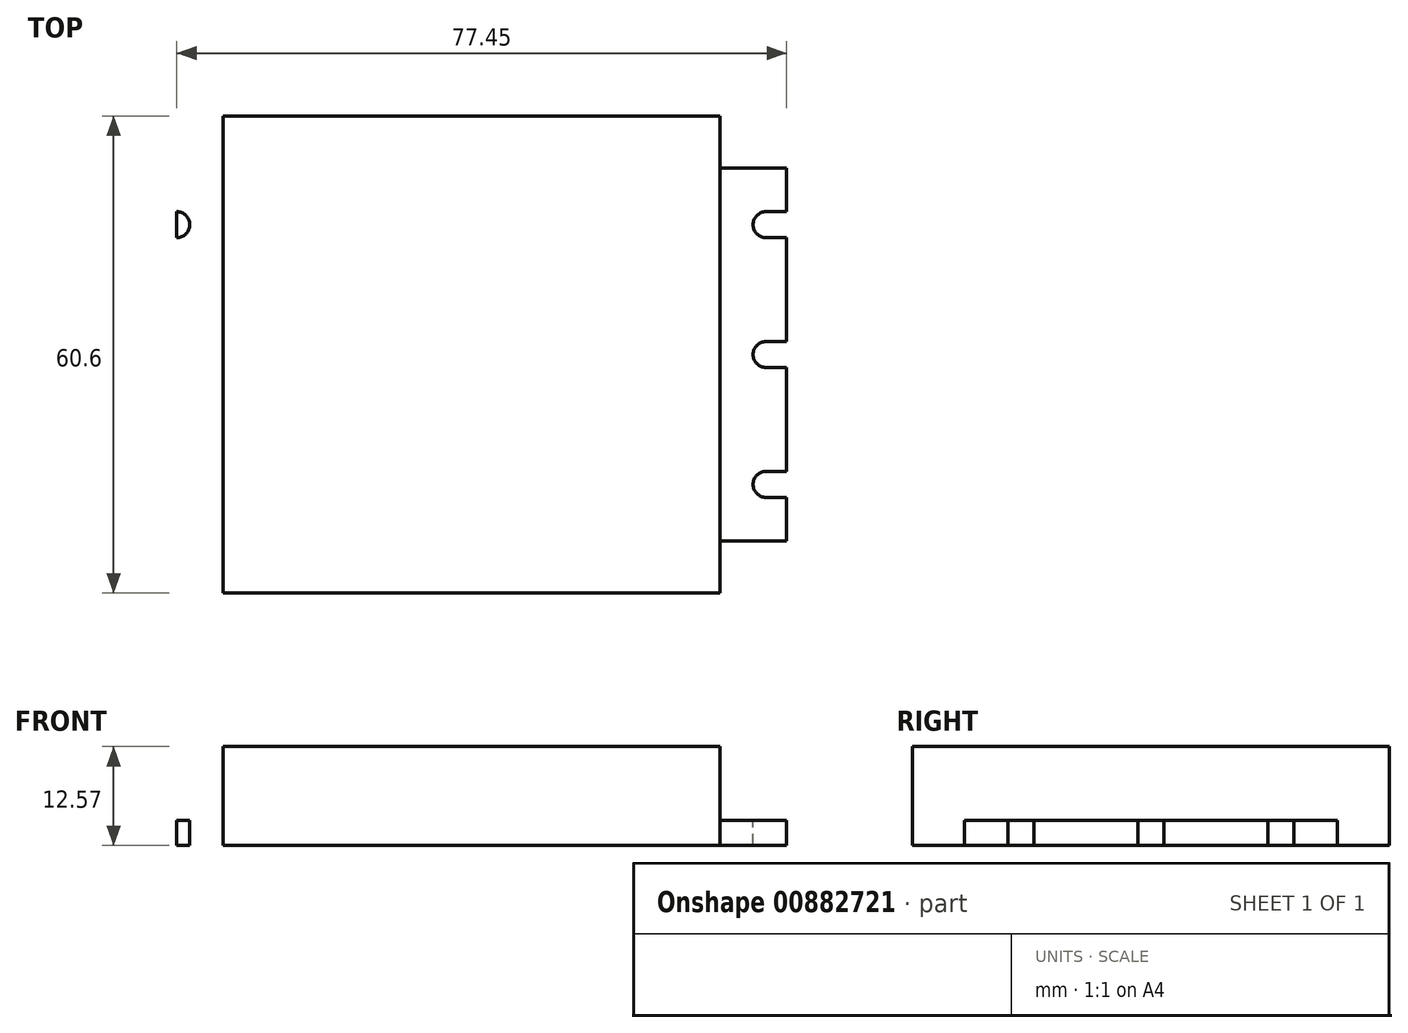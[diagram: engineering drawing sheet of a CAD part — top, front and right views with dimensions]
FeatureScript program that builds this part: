
annotation { "Feature Type Name" : "Feature", "Feature Type Description" : "" }
export const myFeature = defineFeature(function(context is Context, id is Id, definition is map)
    precondition{}
    {
        {
            var Q0;
            Q0=qCreatedBy(makeId("Top.planeOp"),FACE);
            var sketch = newSketch(context, id + "F0", { "sketchPlane" : qUnion([Q0])});
            skLineSegment(sketch, "E0.bottom", {"start": v(31.57, 30.3) * mm, "end": v(-31.57, 30.3) * mm});
            skLineSegment(sketch, "E0.top", {"start": v(31.57, -30.3) * mm, "end": v(-31.57, -30.3) * mm});
            skLineSegment(sketch, "E0.left", {"start": v(31.57, 30.3) * mm, "end": v(31.57, -30.3) * mm});
            skLineSegment(sketch, "E0.right", {"start": v(-31.57, 30.3) * mm, "end": v(-31.57, -30.3) * mm});
            skPoint(sketch, "E0.middle", {"position": v(0, 0) * mm});
            skLineSegment(sketch, "E1.bottom", {"start": v(25.4, 25.4) * mm, "end": v(-25.4, 25.4) * mm, "construction": true});
            skLineSegment(sketch, "E1.top", {"start": v(25.4, -25.4) * mm, "end": v(-25.4, -25.4) * mm, "construction": true});
            skLineSegment(sketch, "E1.left", {"start": v(25.4, 25.4) * mm, "end": v(25.4, -25.4) * mm, "construction": true});
            skLineSegment(sketch, "E1.right", {"start": v(-25.4, 25.4) * mm, "end": v(-25.4, -25.4) * mm, "construction": true});
            skSolve(sketch);
        }
        {
            var Q0;
            Q0=makeQuery(id+"F0.imprint","IMPRINT",FACE,{"disambiguationData":[TD([[makeQuery(id+"F0.imprint","IMPRINT",EDGE,{"derivedFrom":sQuery(id+"F0.wireOp",EDGE,"E0.bottom")}),1.0]])]});
            extrude(context, id + "F1", {"entities" : qUnion([Q0]), "depth" : 12.57 * mm, "offsetDistance" : 25 * mm});
        }
        {
            var Q0;
            Q0=makeQuery(id+"F1.opExtrude","SWEPT_FACE",FACE,{"disambiguationData":[OSD([sQuery(id+"F0.wireOp",EDGE,"E0.right")])]});
            var sketch = newSketch(context, id + "F2", { "sketchPlane" : qUnion([Q0])});
            skLineSegment(sketch, "E2.bottom", {"start": v(-23.7, 3.18) * mm, "end": v(23.7, 3.18) * mm});
            skLineSegment(sketch, "E2.top", {"start": v(-23.7, 0) * mm, "end": v(23.7, 0) * mm});
            skLineSegment(sketch, "E2.left", {"start": v(-23.7, 3.18) * mm, "end": v(-23.7, 0) * mm});
            skLineSegment(sketch, "E2.right", {"start": v(23.7, 3.18) * mm, "end": v(23.7, 0) * mm});
            skSolve(sketch);
        }
        {
            var Q0;
            Q0=makeQuery(id+"F2.imprint","IMPRINT",FACE,{"disambiguationData":[TD([[makeQuery(id+"F2.imprint","IMPRINT",EDGE,{"derivedFrom":sQuery(id+"F2.wireOp",EDGE,"E2.bottom")}),-1.0]])]});
            extrude(context, id + "F3", {"entities" : qUnion([Q0]), "operationType" : NewBodyOperationType.ADD, "depth" : 8.45 * mm, "offsetDistance" : 25 * mm});
        }
        {
            var Q0;
            Q0=makeQuery(id+"F1.opExtrude","SWEPT_BODY",BODY,{"disambiguationData":[OSD([sQuery(id+"F0.wireOp",EDGE,"E0.bottom"),sQuery(id+"F0.wireOp",EDGE,"E0.top"),sQuery(id+"F0.wireOp",EDGE,"E0.left"),sQuery(id+"F0.wireOp",EDGE,"E0.right")])]});
            var Q1;
            Q1=qCreatedBy(makeId("Right.planeOp"),FACE);
            mirror(context, id + "F4", {"operationType" : NewBodyOperationType.ADD, "entities" : qUnion([Q0]), "mirrorPlane" : qUnion([Q1])});
        }
        {
            var Q0;
            Q0=makeQuery(id+"F3.opExtrude","SWEPT_FACE",FACE,{"disambiguationData":[OSD([sQuery(id+"F2.wireOp",EDGE,"E2.bottom")])]});
            var sketch = newSketch(context, id + "F5", { "sketchPlane" : qUnion([Q0])});
            skLineSegment(sketch, "E3", {"start": v(-40.02, 1.65) * mm, "end": v(-37.43, 1.65) * mm});
            skLineSegment(sketch, "E4", {"start": v(-37.43, 1.65) * mm, "end": v(-37.43, -1.65) * mm});
            skLineSegment(sketch, "E5", {"start": v(-37.43, -1.65) * mm, "end": v(-40.02, -1.65) * mm});
            skArc(sketch, "E6", {"start": v(-37.43, 1.65) * mm, "mid": v(-35.78, 0) * mm, "end": v(-37.43, -1.65) * mm});
            skLineSegment(sketch, "E7.0.1.0", {"start": v(-40.02, 18.15) * mm, "end": v(-37.43, 18.15) * mm});
            skArc(sketch, "E7.0.1.1", {"start": v(-37.43, 18.15) * mm, "mid": v(-35.78, 16.5) * mm, "end": v(-37.43, 14.85) * mm});
            skLineSegment(sketch, "E7.0.1.2", {"start": v(-37.43, 14.85) * mm, "end": v(-40.02, 14.85) * mm});
            skLineSegment(sketch, "E7.0.1.3", {"start": v(-37.43, 18.15) * mm, "end": v(-37.43, 14.85) * mm});
            skLineSegment(sketch, "E7.direction1", {"start": v(-40.02, -1.65) * mm, "end": v(-37.92, -1.65) * mm, "construction": true});
            skLineSegment(sketch, "E7.direction2", {"start": v(-40.02, -1.65) * mm, "end": v(-40.02, 14.85) * mm, "construction": true});
            skLineSegment(sketch, "E8.MirrorCS", {"start": v(-37.43, -14.85) * mm, "end": v(-40.02, -14.85) * mm});
            skArc(sketch, "E9.MirrorCS", {"start": v(-37.43, -18.15) * mm, "mid": v(-35.78, -16.5) * mm, "end": v(-37.43, -14.85) * mm});
            skLineSegment(sketch, "E10.MirrorCS", {"start": v(-37.43, -18.15) * mm, "end": v(-37.43, -14.85) * mm});
            skLineSegment(sketch, "E11.MirrorCS", {"start": v(-40.02, -18.15) * mm, "end": v(-37.43, -18.15) * mm});
            skLineSegment(sketch, "E12.MirrorCS", {"start": v(37.43, -1.65) * mm, "end": v(40.02, -1.65) * mm});
            skLineSegment(sketch, "E13.MirrorCS", {"start": v(37.43, 1.65) * mm, "end": v(37.43, -1.65) * mm});
            skLineSegment(sketch, "E14.MirrorCS", {"start": v(37.43, -18.15) * mm, "end": v(37.43, -14.85) * mm});
            skLineSegment(sketch, "E15.MirrorCS", {"start": v(37.43, 18.15) * mm, "end": v(37.43, 14.85) * mm});
            skLineSegment(sketch, "E16.MirrorCS", {"start": v(40.02, -1.65) * mm, "end": v(40.02, 14.85) * mm, "construction": true});
            skLineSegment(sketch, "E17.MirrorCS", {"start": v(40.02, -1.65) * mm, "end": v(37.92, -1.65) * mm, "construction": true});
            skLineSegment(sketch, "E18.MirrorCS", {"start": v(37.43, 14.85) * mm, "end": v(40.02, 14.85) * mm});
            skLineSegment(sketch, "E19.MirrorCS", {"start": v(40.02, 1.65) * mm, "end": v(37.43, 1.65) * mm});
            skLineSegment(sketch, "E20.MirrorCS", {"start": v(37.43, -14.85) * mm, "end": v(40.02, -14.85) * mm});
            skLineSegment(sketch, "E21.MirrorCS", {"start": v(40.02, 18.15) * mm, "end": v(37.43, 18.15) * mm});
            skLineSegment(sketch, "E22.MirrorCS", {"start": v(40.02, -18.15) * mm, "end": v(37.43, -18.15) * mm});
            skArc(sketch, "E23.MirrorCS", {"start": v(37.43, -18.15) * mm, "mid": v(35.78, -16.5) * mm, "end": v(37.43, -14.85) * mm});
            skArc(sketch, "E24.MirrorCS", {"start": v(37.43, 1.65) * mm, "mid": v(35.78, 0) * mm, "end": v(37.43, -1.65) * mm});
            skArc(sketch, "E25.MirrorCS", {"start": v(37.43, 18.15) * mm, "mid": v(35.78, 16.5) * mm, "end": v(37.43, 14.85) * mm});
            skLineSegment(sketch, "E26", {"start": v(40.02, -14.85) * mm, "end": v(40.02, -18.15) * mm});
            skLineSegment(sketch, "E27", {"start": v(40.02, 1.65) * mm, "end": v(40.02, -1.65) * mm});
            skLineSegment(sketch, "E28", {"start": v(40.02, 18.15) * mm, "end": v(40.02, 14.85) * mm});
            skSolve(sketch);
        }
        {
            var Q0;
            {var subQ0=sQuery(id+"F5.wireOp",EDGE,"E7.0.1.0");Q0=makeQuery(id+"F5.imprint","IMPRINT",FACE,{"disambiguationData":[TD([[makeQuery(id+"F5.imprint","IMPRINT",EDGE,{"derivedFrom":subQ0}),-1.0]])]});}
            var Q1;
            Q1=makeQuery(id+"F5.imprint","IMPRINT",FACE,{"disambiguationData":[TD([[makeQuery(id+"F5.imprint","IMPRINT",EDGE,{"derivedFrom":sQuery(id+"F5.wireOp",EDGE,"E7.0.1.1")}),-1.0]])]});
            var Q2;
            {var subQ0=sQuery(id+"F5.wireOp",EDGE,"E3");Q2=makeQuery(id+"F5.imprint","IMPRINT",FACE,{"disambiguationData":[TD([[makeQuery(id+"F5.imprint","IMPRINT",EDGE,{"derivedFrom":subQ0}),-1.0]])]});}
            var Q3;
            Q3=makeQuery(id+"F5.imprint","IMPRINT",FACE,{"disambiguationData":[TD([[makeQuery(id+"F5.imprint","IMPRINT",EDGE,{"derivedFrom":sQuery(id+"F5.wireOp",EDGE,"E4")}),1.0]])]});
            var Q4;
            {var subQ0=sQuery(id+"F5.wireOp",EDGE,"E8.MirrorCS");Q4=makeQuery(id+"F5.imprint","IMPRINT",FACE,{"disambiguationData":[TD([[makeQuery(id+"F5.imprint","IMPRINT",EDGE,{"derivedFrom":subQ0}),1.0]])]});}
            var Q5;
            Q5=makeQuery(id+"F5.imprint","IMPRINT",FACE,{"disambiguationData":[TD([[makeQuery(id+"F5.imprint","IMPRINT",EDGE,{"derivedFrom":sQuery(id+"F5.wireOp",EDGE,"E9.MirrorCS")}),1.0]])]});
            var Q6;
            Q6=makeQuery(id+"F5.imprint","IMPRINT",FACE,{"disambiguationData":[TD([[makeQuery(id+"F5.imprint","IMPRINT",EDGE,{"derivedFrom":sQuery(id+"F5.wireOp",EDGE,"3611b42b-cb9d-4331-b084-d8c496b7ee984.MirrorCS")}),1.0]])]});
            var Q7;
            Q7=makeQuery(id+"F5.imprint","IMPRINT",FACE,{"disambiguationData":[TD([[makeQuery(id+"F5.imprint","IMPRINT",EDGE,{"derivedFrom":sQuery(id+"F5.wireOp",EDGE,"E15.MirrorCS")}),-1.0]])]});
            var Q8;
            Q8=makeQuery(id+"F5.imprint","IMPRINT",FACE,{"disambiguationData":[TD([[makeQuery(id+"F5.imprint","IMPRINT",EDGE,{"derivedFrom":sQuery(id+"F5.wireOp",EDGE,"E15.MirrorCS")}),1.0]])]});
            var Q9;
            Q9=makeQuery(id+"F5.imprint","IMPRINT",FACE,{"disambiguationData":[TD([[makeQuery(id+"F5.imprint","IMPRINT",EDGE,{"derivedFrom":sQuery(id+"F5.wireOp",EDGE,"E13.MirrorCS")}),-1.0]])]});
            var Q10;
            Q10=makeQuery(id+"F5.imprint","IMPRINT",FACE,{"disambiguationData":[TD([[makeQuery(id+"F5.imprint","IMPRINT",EDGE,{"derivedFrom":sQuery(id+"F5.wireOp",EDGE,"E12.MirrorCS")}),1.0]])]});
            var Q11;
            Q11=makeQuery(id+"F5.imprint","IMPRINT",FACE,{"disambiguationData":[TD([[makeQuery(id+"F5.imprint","IMPRINT",EDGE,{"derivedFrom":sQuery(id+"F5.wireOp",EDGE,"E14.MirrorCS")}),1.0]])]});
            var Q12;
            Q12=makeQuery(id+"F5.imprint","IMPRINT",FACE,{"disambiguationData":[TD([[makeQuery(id+"F5.imprint","IMPRINT",EDGE,{"derivedFrom":sQuery(id+"F5.wireOp",EDGE,"E14.MirrorCS")}),-1.0]])]});
            extrude(context, id + "F6", {"entities" : qUnion([Q0, Q1, Q2, Q3, Q4, Q5, Q6, Q7, Q8, Q9, Q10, Q11, Q12]), "operationType" : NewBodyOperationType.REMOVE, "endBound" : BoundingType.UP_TO_NEXT, "oppositeDirection" : true, "depth" : 25 * mm, "offsetDistance" : 25 * mm});
        }
    });
